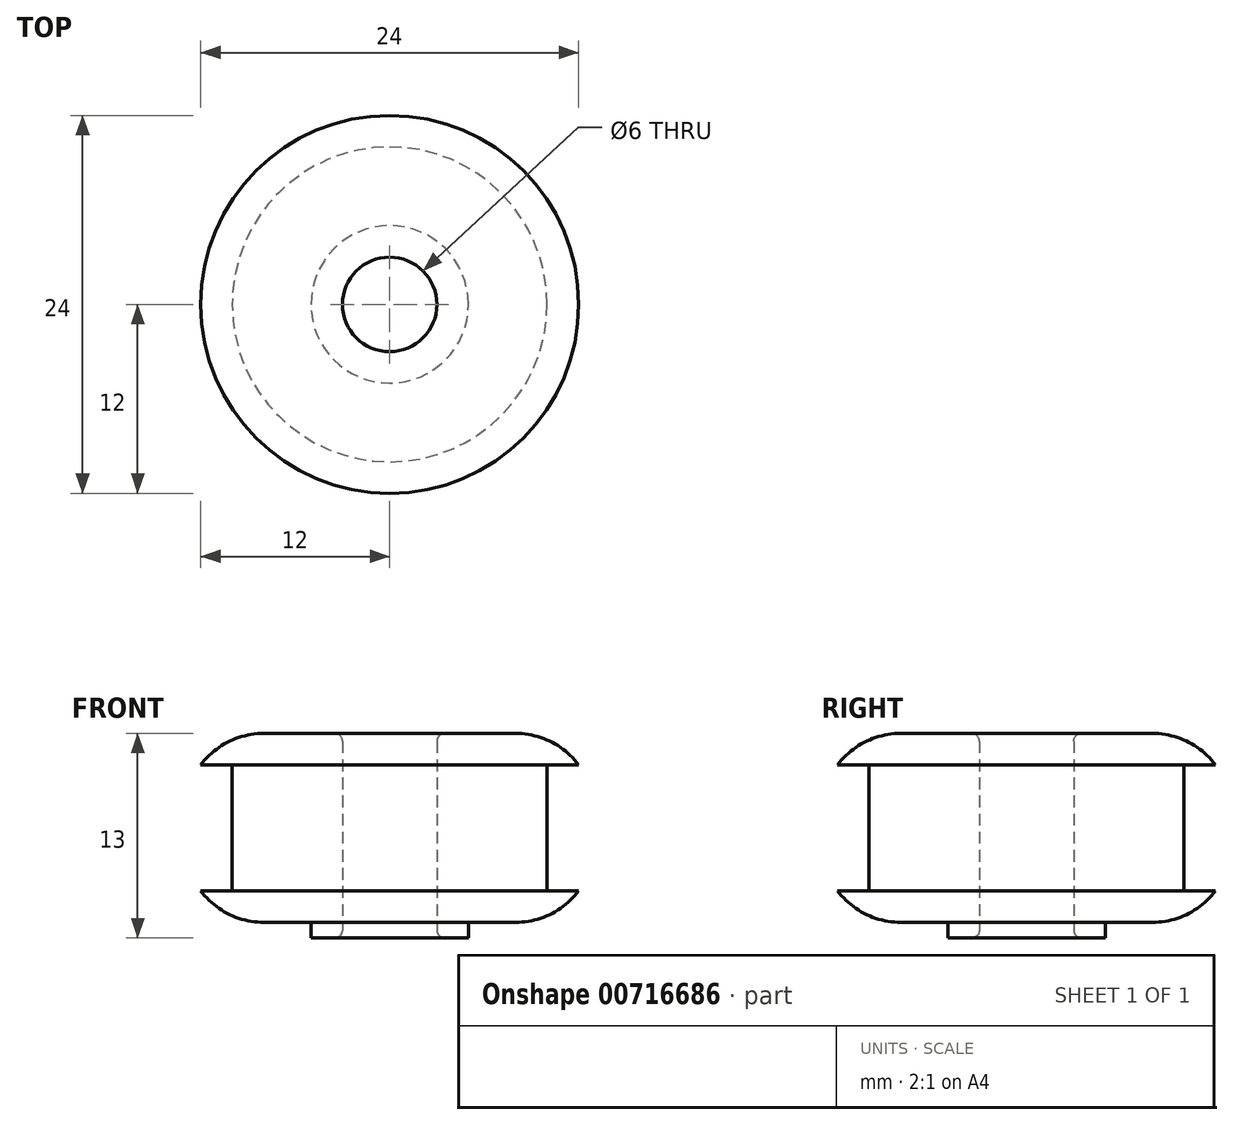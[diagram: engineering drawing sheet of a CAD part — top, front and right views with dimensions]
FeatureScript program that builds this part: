
annotation { "Feature Type Name" : "Feature", "Feature Type Description" : "" }
export const myFeature = defineFeature(function(context is Context, id is Id, definition is map)
    precondition{}
    {
        {
            var Q0;
            Q0=qCreatedBy(makeId("Top.planeOp"),FACE);
            var sketch = newSketch(context, id + "F0", { "sketchPlane" : qUnion([Q0])});
            skCircle(sketch, "E0", {"center": v(0, 0) * mm, "radius": 10 * mm});
            skSolve(sketch);
        }
        {
            var Q0;
            Q0=makeQuery(id+"F0.imprint","IMPRINT",FACE,{"disambiguationData":[TD([[makeQuery(id+"F0.imprint","IMPRINT",EDGE,{"derivedFrom":sQuery(id+"F0.wireOp",EDGE,"E0")}),1.0]])]});
            extrude(context, id + "F1", {"entities" : qUnion([Q0]), "depth" : 8 * mm, "offsetDistance" : 25 * mm});
        }
        {
            var Q0;
            Q0=makeQuery(id+"F1.opExtrude","CAP_FACE",FACE,{"disambiguationData":[OSD([sQuery(id+"F0.wireOp",EDGE,"E0")])],"isStart":false});
            var sketch = newSketch(context, id + "F2", { "sketchPlane" : qUnion([Q0])});
            skCircle(sketch, "E1.0", {"center": v(0, 0) * mm, "radius": 12 * mm});
            skSolve(sketch);
        }
        {
            var Q0;
            Q0=makeQuery(id+"F2.imprint","IMPRINT",FACE,{"disambiguationData":[TD([[makeQuery(id+"F2.imprint","IMPRINT",EDGE,{"derivedFrom":sQuery(id+"F2.wireOp",EDGE,"E1.0")}),1.0]])]});
            var Q1;
            Q1=makeQuery(id+"F2.imprint","IMPRINT",FACE,{"disambiguationData":[TD([[makeQuery(id+"F2.imprint","IMPRINT",EDGE,{"derivedFrom":makeQuery(id+"F1.opExtrude","CAP_EDGE",EDGE,{"disambiguationData":[OSD([sQuery(id+"F0.wireOp",EDGE,"E0")])],"isStart":false})}),1.0]])]});
            extrude(context, id + "F3", {"entities" : qUnion([Q0, Q1]), "depth" : 2 * mm, "offsetDistance" : 25 * mm});
        }
        {
            var Q0;
            Q0=makeQuery(id+"F1.opExtrude","CAP_FACE",FACE,{"disambiguationData":[OSD([sQuery(id+"F0.wireOp",EDGE,"E0")])],"isStart":true});
            var sketch = newSketch(context, id + "F4", { "sketchPlane" : qUnion([Q0])});
            skCircle(sketch, "E2.0", {"center": v(0, 0) * mm, "radius": 12 * mm});
            skSolve(sketch);
        }
        {
            var Q0;
            Q0=makeQuery(id+"F4.imprint","IMPRINT",FACE,{"disambiguationData":[TD([[makeQuery(id+"F4.imprint","IMPRINT",EDGE,{"derivedFrom":sQuery(id+"F4.wireOp",EDGE,"E2.0")}),1.0]])]});
            var Q1;
            Q1=makeQuery(id+"F4.imprint","IMPRINT",FACE,{"disambiguationData":[TD([[makeQuery(id+"F4.imprint","IMPRINT",EDGE,{"derivedFrom":makeQuery(id+"F1.opExtrude","CAP_EDGE",EDGE,{"disambiguationData":[OSD([sQuery(id+"F0.wireOp",EDGE,"E0")])],"isStart":true})}),-1.0]])]});
            extrude(context, id + "F5", {"entities" : qUnion([Q0, Q1]), "operationType" : NewBodyOperationType.ADD, "depth" : 2 * mm, "offsetDistance" : 25 * mm});
        }
        {
            var Q0;
            Q0=makeQuery(id+"F5.opExtrude","CAP_FACE",FACE,{"disambiguationData":[OSD([sQuery(id+"F4.wireOp",EDGE,"E2.0")])],"isStart":false});
            var sketch = newSketch(context, id + "F6", { "sketchPlane" : qUnion([Q0])});
            skCircle(sketch, "E3", {"center": v(0, 0) * mm, "radius": 3 * mm});
            skSolve(sketch);
        }
        {
            var Q0;
            Q0=makeQuery(id+"F6.imprint","IMPRINT",FACE,{"disambiguationData":[TD([[makeQuery(id+"F6.imprint","IMPRINT",EDGE,{"derivedFrom":sQuery(id+"F6.wireOp",EDGE,"E3")}),1.0]])]});
            extrude(context, id + "F7", {"entities" : qUnion([Q0]), "operationType" : NewBodyOperationType.REMOVE, "oppositeDirection" : true, "depth" : 25 * mm, "offsetDistance" : 25 * mm});
        }
        {
            var Q0;
            Q0=makeQuery(id+"F3.opExtrude","SWEPT_BODY",BODY,{"disambiguationData":[OSD([sQuery(id+"F2.wireOp",EDGE,"E1.0")])]});
            var Q1;
            Q1=makeQuery(id+"F1.opExtrude","SWEPT_BODY",BODY,{"disambiguationData":[OSD([sQuery(id+"F0.wireOp",EDGE,"E0")])]});
            booleanBodies(context, id + "F8", {"operationType" : BooleanOperationType.UNION, "tools" : qUnion([Q0, Q1])});
        }
        {
            var Q0;
            Q0=makeQuery(id+"F5.opExtrude","CAP_FACE",FACE,{"disambiguationData":[OSD([sQuery(id+"F4.wireOp",EDGE,"E2.0")])],"isStart":false});
            var sketch = newSketch(context, id + "F9", { "sketchPlane" : qUnion([Q0])});
            skCircle(sketch, "E4.0", {"center": v(0, 0) * mm, "radius": 5 * mm});
            skCircle(sketch, "E5.0", {"center": v(0, 0) * mm, "radius": 17 * mm});
            skSolve(sketch);
        }
        {
            var Q0;
            Q0=makeQuery(id+"F9.imprint","IMPRINT",FACE,{"disambiguationData":[TD([[makeQuery(id+"F9.imprint","IMPRINT",EDGE,{"derivedFrom":sQuery(id+"F9.wireOp",EDGE,"E4.0")}),1.0]])]});
            extrude(context, id + "F10", {"entities" : qUnion([Q0]), "operationType" : NewBodyOperationType.ADD, "depth" : 1 * mm, "offsetDistance" : 25 * mm});
        }
        {
            var Q0;
            Q0=makeQuery(id+"F10.opExtrude","CAP_EDGE",EDGE,{"disambiguationData":[OSD([sQuery(id+"F6.wireOp",EDGE,"E3")])],"isStart":false});
            fillet(context, id + "F11", {"entities" : qUnion([Q0]), "radius" : 0.5 * mm, "tangentPropagation" : true, "allowEdgeOverflow" : false});
        }
        {
            var Q0;
            Q0=makeQuery(id+"F5.opExtrude","CAP_EDGE",EDGE,{"disambiguationData":[OSD([sQuery(id+"F4.wireOp",EDGE,"E2.0")])],"isStart":false});
            var Q1;
            Q1=makeQuery(id+"F3.opExtrude","CAP_EDGE",EDGE,{"disambiguationData":[OSD([sQuery(id+"F2.wireOp",EDGE,"E1.0")])],"isStart":false});
            fillet(context, id + "F12", {"entities" : qUnion([Q0, Q1]), "radius" : 5 * mm, "tangentPropagation" : true, "allowEdgeOverflow" : false});
        }
        {
            var Q0;
            {var subQ0=sQuery(id+"F6.wireOp",EDGE,"E3");var subQ1=sQuery(id+"F2.wireOp",EDGE,"E1.0");var subQ2=makeQuery(id+"F7.opExtrude","SWEPT_FACE",FACE,{"disambiguationData":[OSD([subQ0])]});Q0=makeQuery(id+"F10.boolean.opBoolean","MERGE",FACE,{"derivedFrom":[makeQuery(id+"F8.opBoolean","MERGE",FACE,{"derivedFrom":[makeQuery(id+"F7.boolean.opBoolean","COPY",FACE,{"disambiguationData":[TD([makeQuery(id+"F1.opExtrude","CAP_FACE",FACE,{"disambiguationData":[OSD([sQuery(id+"F0.wireOp",EDGE,"E0")])],"isStart":false})])],"derivedFrom":subQ2}),makeQuery(id+"F7.boolean.opBoolean","COPY",FACE,{"disambiguationData":[TD([makeQuery(id+"F3.opExtrude","CAP_FACE",FACE,{"disambiguationData":[OSD([subQ1])],"isStart":true})])],"derivedFrom":subQ2})]}),makeQuery(id+"F10.opExtrude","SWEPT_FACE",FACE,{"disambiguationData":[OSD([subQ0])]})]});}
            fillet(context, id + "F13", {"entities" : qUnion([Q0]), "radius" : 0.5 * mm, "tangentPropagation" : true, "allowEdgeOverflow" : false});
        }
    });
